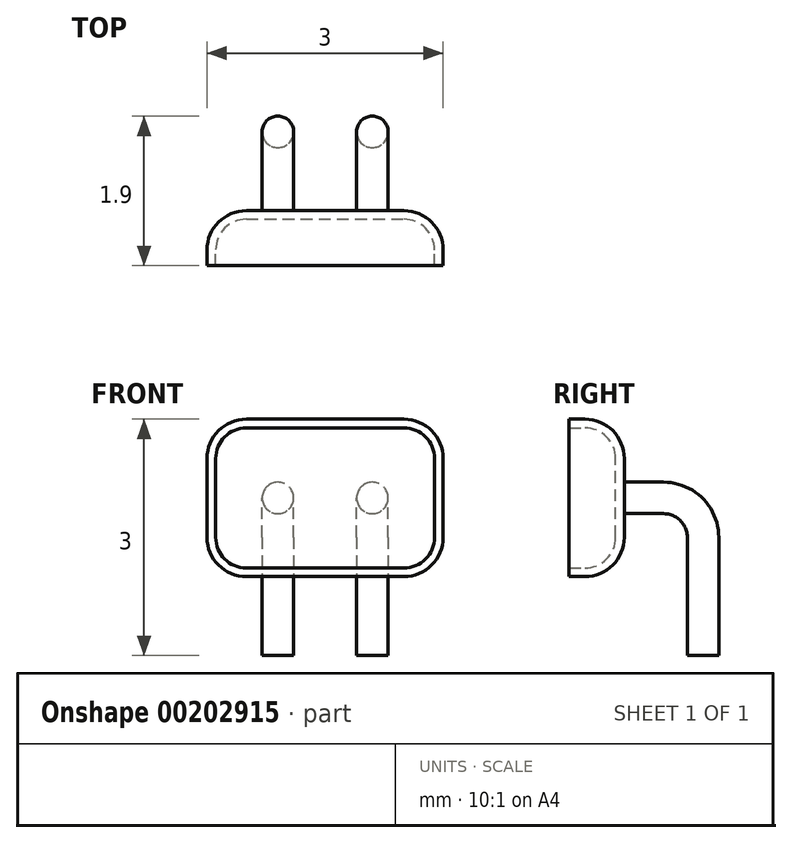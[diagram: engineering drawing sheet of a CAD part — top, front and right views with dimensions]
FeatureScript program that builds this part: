
annotation { "Feature Type Name" : "Feature", "Feature Type Description" : "" }
export const myFeature = defineFeature(function(context is Context, id is Id, definition is map)
    precondition{}
    {
        {
            var Q0;
            Q0=qCreatedBy(makeId("Front.planeOp"),FACE);
            var sketch = newSketch(context, id + "F0", { "sketchPlane" : qUnion([Q0])});
            skLineSegment(sketch, "E0.bottom", {"start": v(0.5, 0) * mm, "end": v(2.5, 0) * mm});
            skLineSegment(sketch, "E0.top", {"start": v(0.5, 2) * mm, "end": v(2.5, 2) * mm});
            skLineSegment(sketch, "E0.left", {"start": v(0, 0.5) * mm, "end": v(0, 1.5) * mm});
            skLineSegment(sketch, "E0.right", {"start": v(3, 0.5) * mm, "end": v(3, 1.5) * mm});
            skPoint(sketch, "E1.visualSharp", {"position": v(0, 2) * mm});
            skArc(sketch, "E1.filletArc", {"start": v(0.5, 2) * mm, "mid": v(0.15, 1.85) * mm, "end": v(0, 1.5) * mm});
            skPoint(sketch, "E2.visualSharp", {"position": v(3, 2) * mm});
            skArc(sketch, "E2.filletArc", {"start": v(3, 1.5) * mm, "mid": v(2.85, 1.85) * mm, "end": v(2.5, 2) * mm});
            skPoint(sketch, "E3.visualSharp", {"position": v(3, 0) * mm});
            skArc(sketch, "E3.filletArc", {"start": v(2.5, 0) * mm, "mid": v(2.85, 0.15) * mm, "end": v(3, 0.5) * mm});
            skPoint(sketch, "E4.visualSharp", {"position": v(0, 0) * mm});
            skArc(sketch, "E4.filletArc", {"start": v(0, 0.5) * mm, "mid": v(0.15, 0.15) * mm, "end": v(0.5, 0) * mm});
            skSolve(sketch);
        }
        {
            var Q0;
            Q0 = qSketchRegion(id + "F0", true);
            extrude(context, id + "F1", {"entities" : qUnion([Q0]), "depth" : .7 * mm});
        }
        {
            var Q0;
            Q0=makeQuery(id+"F1.opExtrude","CAP_FACE",FACE,{"disambiguationData":[OSD([sQuery(id+"F0.wireOp",EDGE,"E0.bottom"),sQuery(id+"F0.wireOp",EDGE,"E0.top"),sQuery(id+"F0.wireOp",EDGE,"E0.left"),sQuery(id+"F0.wireOp",EDGE,"E0.right"),sQuery(id+"F0.wireOp",EDGE,"E1.filletArc"),sQuery(id+"F0.wireOp",EDGE,"E2.filletArc"),sQuery(id+"F0.wireOp",EDGE,"E3.filletArc"),sQuery(id+"F0.wireOp",EDGE,"E4.filletArc")])],"isStart":true});
            fillet(context, id + "F2", {"entities" : qUnion([Q0]), "radius" : .5 * mm, "tangentPropagation" : true, "allowEdgeOverflow" : false});
        }
        {
            var Q0;
            Q0=makeQuery(id+"F1.opExtrude","CAP_FACE",FACE,{"disambiguationData":[OSD([sQuery(id+"F0.wireOp",EDGE,"E0.bottom"),sQuery(id+"F0.wireOp",EDGE,"E0.top"),sQuery(id+"F0.wireOp",EDGE,"E0.left"),sQuery(id+"F0.wireOp",EDGE,"E0.right"),sQuery(id+"F0.wireOp",EDGE,"E1.filletArc"),sQuery(id+"F0.wireOp",EDGE,"E2.filletArc"),sQuery(id+"F0.wireOp",EDGE,"E3.filletArc"),sQuery(id+"F0.wireOp",EDGE,"E4.filletArc")])],"isStart":false});
            shell(context, id + "F3", {"entities" : qUnion([Q0]), "thickness" : .11 * mm});
        }
        {
            var Q0;
            Q0=qCreatedBy(makeId("Right.planeOp"),FACE);
            cPlane(context, id + "F4", {"entities" : qUnion([Q0]), "cplaneType" : CPlaneType.OFFSET, "offset" : 1.5 * mm, "width" : 150 * mm, "height" : 150 * mm});
        }
        {
            var Q0;
            Q0=qCreatedBy(id+"F4.planeOp",FACE);
            var sketch = newSketch(context, id + "F5", { "sketchPlane" : qUnion([Q0])});
            skLineSegment(sketch, "E5", {"start": v(0, 0) * mm, "end": v(0, 2) * mm, "construction": true});
            skLineSegment(sketch, "E6", {"start": v(0, 1) * mm, "end": v(0.5, 1) * mm});
            skLineSegment(sketch, "E7", {"start": v(1, 0.5) * mm, "end": v(1, -1) * mm});
            skPoint(sketch, "E8.visualSharp", {"position": v(1, 1) * mm});
            skArc(sketch, "E8.filletArc", {"start": v(1, 0.5) * mm, "mid": v(0.85, 0.85) * mm, "end": v(0.5, 1) * mm});
            skSolve(sketch);
        }
        {
            var Q0;
            Q0=makeQuery(id+"F1.opExtrude","CAP_FACE",FACE,{"disambiguationData":[OSD([sQuery(id+"F0.wireOp",EDGE,"E0.bottom"),sQuery(id+"F0.wireOp",EDGE,"E0.top"),sQuery(id+"F0.wireOp",EDGE,"E0.left"),sQuery(id+"F0.wireOp",EDGE,"E0.right"),sQuery(id+"F0.wireOp",EDGE,"E1.filletArc"),sQuery(id+"F0.wireOp",EDGE,"E2.filletArc"),sQuery(id+"F0.wireOp",EDGE,"E3.filletArc"),sQuery(id+"F0.wireOp",EDGE,"E4.filletArc")])],"isStart":true});
            var sketch = newSketch(context, id + "F6", { "sketchPlane" : qUnion([Q0])});
            skLineSegment(sketch, "E9", {"start": v(-2.5, 1) * mm, "end": v(-0.5, 1) * mm, "construction": true});
            skCircle(sketch, "E10", {"center": v(-2.1, 1) * mm, "radius": 0.2 * mm});
            skCircle(sketch, "E11", {"center": v(-0.9, 1) * mm, "radius": 0.2 * mm});
            skSolve(sketch);
        }
        {
            var Q0;
            Q0=makeQuery(id+"F6.imprint","IMPRINT",FACE,{"disambiguationData":[TD([[makeQuery(id+"F6.imprint","IMPRINT",EDGE,{"derivedFrom":sQuery(id+"F6.wireOp",EDGE,"E10")}),1.0]])]});
            var Q1;
            Q1=makeQuery(id+"F6.imprint","IMPRINT",FACE,{"disambiguationData":[TD([[makeQuery(id+"F6.imprint","IMPRINT",EDGE,{"derivedFrom":sQuery(id+"F6.wireOp",EDGE,"E11")}),1.0]])]});
            var Q2;
            Q2=sQuery(id+"F5.wireOp",EDGE,"E7");
            var Q3;
            Q3=sQuery(id+"F5.wireOp",EDGE,"E8.filletArc");
            var Q4;
            Q4=sQuery(id+"F5.wireOp",EDGE,"E6");
            sweep(context, id + "F7", {"operationType" : NewBodyOperationType.ADD, "profiles" : qUnion([Q0, Q1]), "path" : qUnion([Q2, Q3, Q4])});
        }
    });
